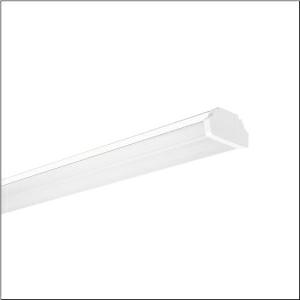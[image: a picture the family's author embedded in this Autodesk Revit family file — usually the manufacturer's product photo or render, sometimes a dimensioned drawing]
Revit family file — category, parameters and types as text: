
# Revit family: modario_31_gen_2_53bm812mv4fxd2_69c1
name_source: partatom
category: Lighting Fixtures
units: mm (PartAtom-declared; Revit-internal decimal feet)

## family parameters
Cut with Voids When Loaded = No
Host = Face
Light Source = No
Part Type = Normal
Room Calculation Point = No
Round Connector Dimension = Use Diameter
Shared = No

## types (1)
- --- (1 x LED, 15440 lm, 82.3 W, 4000K)
    Apparent Load = 82 VA
    CIE Flux Codes = 47 80 95 93 100
    Color Rendering = 80
    Color Temperature = 4000K
    Default Elevation = 1800 mm
    Description = Modario 31 Gen.2, luminaire insert, of sheet steel, coil coated, white, length: 1.495mm, width: 81mm, height: 82mm, 5x system unit, system units: 299mm, LED rated luminous flux: 15.440lm, light colour: 840, SDCM (Standard Deviation of Colour Matching)MacAdam ≤ 3 SDCM (initial), control gear: ON/OFF Multilumen, control gear: ECG, with plug, 3-pole, with phase selection, mains connection: 220..240V, AC, 50/60Hz, rated input power: 82W, through-wiring accessed according to module size, primary optical cover: cover, of PMMA, light emission: direct distribution, primary light characteristic: symmetric, protection rating (complete): IP20, protection rating (LED compartment): IP50, insulation class (complete): insulation class I (protective earthing), certification: CE, ENEC, VDE, UKCA, impact resistance: IK03, permissible ambient temperature for indoor applications: -35..+35°C, corresponds to IFS (International Featured Standards) requirements for safety and quality in the food industry, reducing of maximum allowable ambient temperature of 5°C with ceiling mounting, IP40 when using the optional accessory 5TP9018, packaging unit: 1 piece
    Height = 92 mm
    Lamp = 1 x LED
    Lamp Light Flux = 15440 lm
    Lamp Power = 82.3 W
    Lamp count = 1
    Length = 1495 mm
    Luminous efficacy = 188 lm/W
    Manufacturer = Siteco
    ModVariant = No
    Model = 53BM812MV4FXD2
    Mounting Place = Ceiling
    Mounting Type = Pendant
    Number of Poles = 1
    OnlyDefault = Yes
    Power Factor = 1
    Product Name = Modario 31 Gen.2
    Product group = luminaire insert | ceiling pendant
    ProductGroupID = 901
    Protection Class = Protection class I
    Protection Degree = IP 20
    RLX_Detail_Level = 1
    RLX_Emergency_Light_Flux = 0 lm
    RLX_Emergency_Type = 0
    RLX_Emergency_Type_DB = No
    RlxData = <blob elided: 39781 chars, md5=d0ff9571>
    Socket = socket
    Standby Power = 0 W
    System Light Flux = 15440 lm
    System Power = 82 W
    Type Comments = factory setting: luminous flux: 100 % | (A | C | E) | 193 mA
    Type Image = l_1341886.jpg
    URL = http://relux.com
    VarID = @adj_052379
    Voltage = 0 V
    Weight = 0.00 kg
    Width = 81 mm

## geometry (parser evidence)
native form markers: Blend x4, Sweep x11
no freeform markers — native parametric forms only
